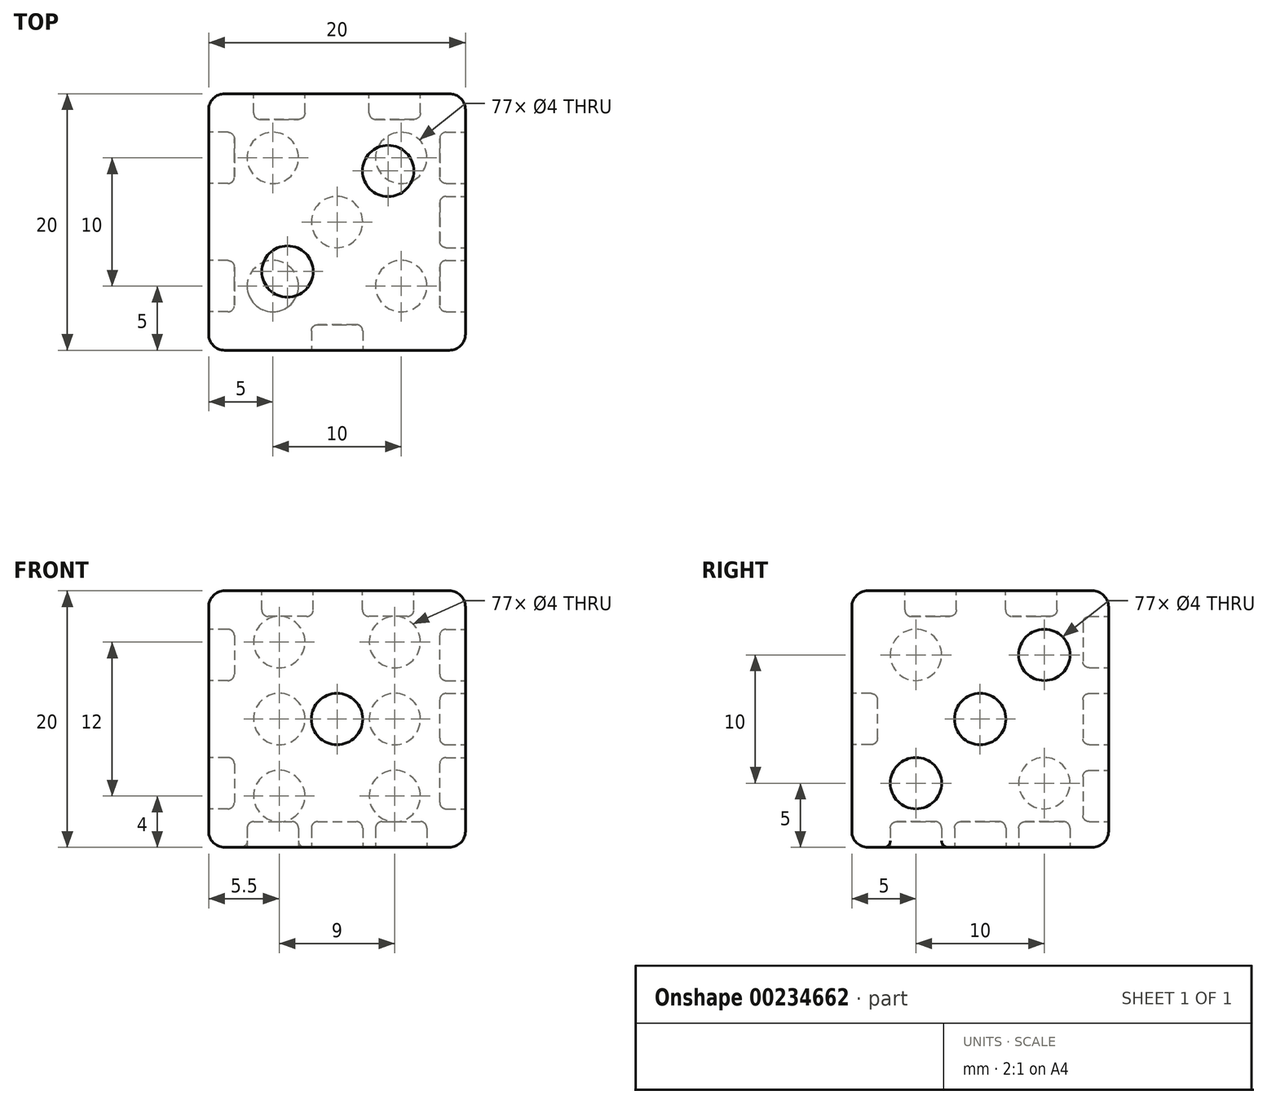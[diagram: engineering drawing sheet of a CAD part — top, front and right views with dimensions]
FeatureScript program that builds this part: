
annotation { "Feature Type Name" : "Feature", "Feature Type Description" : "" }
export const myFeature = defineFeature(function(context is Context, id is Id, definition is map)
    precondition{}
    {
        {
            assignVariable(context, id + "F0", {"name" : "Size", "anyValue" : 20});
        }
        {
            assignVariable(context, id + "F1", {"name" : "HoleDepth", "anyValue" : 2});
        }
        {
            var Q0;
            Q0=qCreatedBy(makeId("Top.planeOp"),FACE);
            var sketch = newSketch(context, id + "F2", { "sketchPlane" : qUnion([Q0])});
            skLineSegment(sketch, "E0.bottom", {"start": v(10, 10) * mm, "end": v(-10, 10) * mm});
            skLineSegment(sketch, "E0.top", {"start": v(10, -10) * mm, "end": v(-10, -10) * mm});
            skLineSegment(sketch, "E0.left", {"start": v(10, 10) * mm, "end": v(10, -10) * mm});
            skLineSegment(sketch, "E0.right", {"start": v(-10, 10) * mm, "end": v(-10, -10) * mm});
            skPoint(sketch, "E0.middle", {"position": v(0, 0) * mm});
            skSolve(sketch);
        }
        {
            var Q0;
            Q0=makeQuery(id+"F2.imprint","IMPRINT",FACE,{"disambiguationData":[TD([[makeQuery(id+"F2.imprint","IMPRINT",EDGE,{"derivedFrom":sQuery(id+"F2.wireOp",EDGE,"E0.bottom")}),1.0]])]});
            extrude(context, id + "F3", {"entities" : qUnion([Q0]), "depth" : (getVariable(context, 'Size')) * mm});
        }
        {
            var Q0;
            Q0=makeQuery(id+"F3.opExtrude","SWEPT_FACE",FACE,{"disambiguationData":[OSD([sQuery(id+"F2.wireOp",EDGE,"E0.top")])]});
            var sketch = newSketch(context, id + "F4", { "sketchPlane" : qUnion([Q0])});
            skLineSegment(sketch, "E1", {"start": v(-10, 20) * mm, "end": v(10, 0) * mm, "construction": true});
            skLineSegment(sketch, "E2", {"start": v(10, 20) * mm, "end": v(-10, 0) * mm, "construction": true});
            skCircle(sketch, "E3", {"center": v(0, 10) * mm, "radius": 2 * mm});
            skSolve(sketch);
        }
        {
            var Q0;
            Q0=makeQuery(id+"F3.opExtrude","CAP_FACE",FACE,{"disambiguationData":[OSD([sQuery(id+"F2.wireOp",EDGE,"E0.bottom"),sQuery(id+"F2.wireOp",EDGE,"E0.top"),sQuery(id+"F2.wireOp",EDGE,"E0.left"),sQuery(id+"F2.wireOp",EDGE,"E0.right")])],"isStart":false});
            var sketch = newSketch(context, id + "F5", { "sketchPlane" : qUnion([Q0])});
            skCircle(sketch, "E4", {"center": v(3.98, 3.98) * mm, "radius": 2 * mm});
            skCircle(sketch, "E5", {"center": v(-3.86, -3.86) * mm, "radius": 2 * mm});
            skLineSegment(sketch, "E6", {"start": v(10, 10) * mm, "end": v(3.98, 3.98) * mm, "construction": true});
            skLineSegment(sketch, "E7", {"start": v(-3.86, -3.86) * mm, "end": v(-10, -10) * mm, "construction": true});
            skLineSegment(sketch, "E8", {"start": v(-3.86, -3.86) * mm, "end": v(3.98, 3.98) * mm, "construction": true});
            skSolve(sketch);
        }
        {
            var Q0;
            Q0=makeQuery(id+"F3.opExtrude","SWEPT_FACE",FACE,{"disambiguationData":[OSD([sQuery(id+"F2.wireOp",EDGE,"E0.bottom")])]});
            var sketch = newSketch(context, id + "F6", { "sketchPlane" : qUnion([Q0])});
            skLineSegment(sketch, "E9.bottom", {"start": v(-4.5, 16) * mm, "end": v(4.5, 16) * mm, "construction": true});
            skLineSegment(sketch, "E9.top", {"start": v(-4.5, 4) * mm, "end": v(4.5, 4) * mm, "construction": true});
            skLineSegment(sketch, "E9.left", {"start": v(-4.5, 16) * mm, "end": v(-4.5, 4) * mm, "construction": true});
            skLineSegment(sketch, "E9.right", {"start": v(4.5, 16) * mm, "end": v(4.5, 4) * mm, "construction": true});
            skLineSegment(sketch, "E10", {"start": v(4.5, 16) * mm, "end": v(10, 20) * mm, "construction": true});
            skLineSegment(sketch, "E11", {"start": v(-4.5, 16) * mm, "end": v(-10, 20) * mm, "construction": true});
            skLineSegment(sketch, "E12", {"start": v(-4.5, 4) * mm, "end": v(-10, 0) * mm, "construction": true});
            skLineSegment(sketch, "E13", {"start": v(4.5, 4) * mm, "end": v(10, 0) * mm, "construction": true});
            skCircle(sketch, "E14", {"center": v(4.5, 4) * mm, "radius": 2 * mm});
            skCircle(sketch, "E15", {"center": v(4.5, 16) * mm, "radius": 2 * mm});
            skCircle(sketch, "E16", {"center": v(-4.5, 16) * mm, "radius": 2 * mm});
            skCircle(sketch, "E17", {"center": v(-4.5, 4) * mm, "radius": 2 * mm});
            skCircle(sketch, "E18", {"center": v(-4.5, 10) * mm, "radius": 2 * mm});
            skCircle(sketch, "E19", {"center": v(4.5, 10) * mm, "radius": 2 * mm});
            skSolve(sketch);
        }
        {
            var Q0;
            Q0=makeQuery(id+"F3.opExtrude","CAP_FACE",FACE,{"disambiguationData":[OSD([sQuery(id+"F2.wireOp",EDGE,"E0.bottom"),sQuery(id+"F2.wireOp",EDGE,"E0.top"),sQuery(id+"F2.wireOp",EDGE,"E0.left"),sQuery(id+"F2.wireOp",EDGE,"E0.right")])],"isStart":true});
            var sketch = newSketch(context, id + "F7", { "sketchPlane" : qUnion([Q0])});
            skCircle(sketch, "E20", {"center": v(0, 0) * mm, "radius": 2 * mm});
            skCircle(sketch, "E21", {"center": v(5, 5) * mm, "radius": 2 * mm});
            skCircle(sketch, "E22", {"center": v(-5, 5) * mm, "radius": 2 * mm});
            skCircle(sketch, "E23", {"center": v(-5, -5) * mm, "radius": 2 * mm});
            skCircle(sketch, "E24", {"center": v(5, -5) * mm, "radius": 2 * mm});
            skLineSegment(sketch, "E25", {"start": v(10, -10) * mm, "end": v(5, -5) * mm, "construction": true});
            skLineSegment(sketch, "E26", {"start": v(0, 0) * mm, "end": v(5, -5) * mm, "construction": true});
            skLineSegment(sketch, "E27", {"start": v(0, 0) * mm, "end": v(-5, 5) * mm, "construction": true});
            skLineSegment(sketch, "E28", {"start": v(-10, 10) * mm, "end": v(-5, 5) * mm, "construction": true});
            skLineSegment(sketch, "E29", {"start": v(10, 10) * mm, "end": v(5, 5) * mm, "construction": true});
            skLineSegment(sketch, "E30", {"start": v(0, 0) * mm, "end": v(5, 5) * mm, "construction": true});
            skLineSegment(sketch, "E31", {"start": v(0, 0) * mm, "end": v(-5, -5) * mm, "construction": true});
            skLineSegment(sketch, "E32", {"start": v(-5, -5) * mm, "end": v(-10, -10) * mm, "construction": true});
            skSolve(sketch);
        }
        {
            var Q0;
            Q0=makeQuery(id+"F3.opExtrude","SWEPT_FACE",FACE,{"disambiguationData":[OSD([sQuery(id+"F2.wireOp",EDGE,"E0.left")])]});
            var sketch = newSketch(context, id + "F8", { "sketchPlane" : qUnion([Q0])});
            skCircle(sketch, "E33", {"center": v(0, 10) * mm, "radius": 2 * mm});
            skCircle(sketch, "E34", {"center": v(5, 15) * mm, "radius": 2 * mm});
            skCircle(sketch, "E35", {"center": v(-5, 5) * mm, "radius": 2 * mm});
            skLineSegment(sketch, "E36", {"start": v(10, 20) * mm, "end": v(5, 15) * mm, "construction": true});
            skLineSegment(sketch, "E37", {"start": v(0, 10) * mm, "end": v(5, 15) * mm, "construction": true});
            skLineSegment(sketch, "E38", {"start": v(0, 10) * mm, "end": v(-5, 5) * mm, "construction": true});
            skLineSegment(sketch, "E39", {"start": v(-5, 5) * mm, "end": v(-10, 0) * mm, "construction": true});
            skSolve(sketch);
        }
        {
            var Q0;
            Q0=makeQuery(id+"F3.opExtrude","SWEPT_FACE",FACE,{"disambiguationData":[OSD([sQuery(id+"F2.wireOp",EDGE,"E0.right")])]});
            var sketch = newSketch(context, id + "F9", { "sketchPlane" : qUnion([Q0])});
            skLineSegment(sketch, "E40", {"start": v(10, 20) * mm, "end": v(-10, 0) * mm, "construction": true});
            skLineSegment(sketch, "E41", {"start": v(-10, 20) * mm, "end": v(10, 0) * mm, "construction": true});
            skLineSegment(sketch, "E42.bottom", {"start": v(-5, 15) * mm, "end": v(5, 15) * mm, "construction": true});
            skLineSegment(sketch, "E42.top", {"start": v(-5, 5) * mm, "end": v(5, 5) * mm, "construction": true});
            skLineSegment(sketch, "E42.left", {"start": v(-5, 15) * mm, "end": v(-5, 5) * mm, "construction": true});
            skLineSegment(sketch, "E42.right", {"start": v(5, 15) * mm, "end": v(5, 5) * mm, "construction": true});
            skPoint(sketch, "E42.middle", {"position": v(0, 10) * mm});
            skCircle(sketch, "E43", {"center": v(5, 15) * mm, "radius": 2 * mm});
            skCircle(sketch, "E44", {"center": v(5, 5) * mm, "radius": 2 * mm});
            skCircle(sketch, "E45", {"center": v(-5, 5) * mm, "radius": 2 * mm});
            skCircle(sketch, "E46", {"center": v(-5, 15) * mm, "radius": 2 * mm});
            skLineSegment(sketch, "E47", {"start": v(10, 10) * mm, "end": v(5, 5) * mm, "construction": true});
            skLineSegment(sketch, "E48", {"start": v(0, 0) * mm, "end": v(5, 5) * mm, "construction": true});
            skSolve(sketch);
        }
        {
            var Q0;
            Q0=makeQuery(id+"F4.imprint","IMPRINT",FACE,{"disambiguationData":[TD([[makeQuery(id+"F4.imprint","IMPRINT",EDGE,{"derivedFrom":sQuery(id+"F4.wireOp",EDGE,"E3")}),1.0]])]});
            extrude(context, id + "F10", {"entities" : qUnion([Q0]), "operationType" : NewBodyOperationType.REMOVE, "oppositeDirection" : true, "depth" : (getVariable(context, 'HoleDepth')) * mm});
        }
        {
            var Q0;
            Q0=makeQuery(id+"F5.imprint","IMPRINT",FACE,{"disambiguationData":[TD([[makeQuery(id+"F5.imprint","IMPRINT",EDGE,{"derivedFrom":sQuery(id+"F5.wireOp",EDGE,"E5")}),1.0]])]});
            var Q1;
            Q1=makeQuery(id+"F5.imprint","IMPRINT",FACE,{"disambiguationData":[TD([[makeQuery(id+"F5.imprint","IMPRINT",EDGE,{"derivedFrom":sQuery(id+"F5.wireOp",EDGE,"E4")}),1.0]])]});
            extrude(context, id + "F11", {"entities" : qUnion([Q0, Q1]), "operationType" : NewBodyOperationType.REMOVE, "oppositeDirection" : true, "depth" : (getVariable(context, 'HoleDepth')) * mm});
        }
        {
            var Q0;
            Q0=makeQuery(id+"F8.imprint","IMPRINT",FACE,{"disambiguationData":[TD([[makeQuery(id+"F8.imprint","IMPRINT",EDGE,{"derivedFrom":sQuery(id+"F8.wireOp",EDGE,"E35")}),1.0]])]});
            var Q1;
            Q1=makeQuery(id+"F8.imprint","IMPRINT",FACE,{"disambiguationData":[TD([[makeQuery(id+"F8.imprint","IMPRINT",EDGE,{"derivedFrom":sQuery(id+"F8.wireOp",EDGE,"E34")}),1.0]])]});
            var Q2;
            Q2=makeQuery(id+"F8.imprint","IMPRINT",FACE,{"disambiguationData":[TD([[makeQuery(id+"F8.imprint","IMPRINT",EDGE,{"derivedFrom":sQuery(id+"F8.wireOp",EDGE,"E33")}),1.0]])]});
            extrude(context, id + "F12", {"entities" : qUnion([Q0, Q1, Q2]), "operationType" : NewBodyOperationType.REMOVE, "oppositeDirection" : true, "depth" : (getVariable(context, 'HoleDepth')) * mm});
        }
        {
            var Q0;
            Q0=makeQuery(id+"F9.imprint","IMPRINT",FACE,{"disambiguationData":[TD([[makeQuery(id+"F9.imprint","IMPRINT",EDGE,{"derivedFrom":sQuery(id+"F9.wireOp",EDGE,"E46")}),1.0]])]});
            var Q1;
            Q1=makeQuery(id+"F9.imprint","IMPRINT",FACE,{"disambiguationData":[TD([[makeQuery(id+"F9.imprint","IMPRINT",EDGE,{"derivedFrom":sQuery(id+"F9.wireOp",EDGE,"E43")}),1.0]])]});
            var Q2;
            Q2=makeQuery(id+"F9.imprint","IMPRINT",FACE,{"disambiguationData":[TD([[makeQuery(id+"F9.imprint","IMPRINT",EDGE,{"derivedFrom":sQuery(id+"F9.wireOp",EDGE,"E44")}),1.0]])]});
            var Q3;
            Q3=makeQuery(id+"F9.imprint","IMPRINT",FACE,{"disambiguationData":[TD([[makeQuery(id+"F9.imprint","IMPRINT",EDGE,{"derivedFrom":sQuery(id+"F9.wireOp",EDGE,"E45")}),1.0]])]});
            extrude(context, id + "F13", {"entities" : qUnion([Q0, Q1, Q2, Q3]), "operationType" : NewBodyOperationType.REMOVE, "oppositeDirection" : true, "offsetDistance" : 25 * mm, "depth" : (getVariable(context, 'HoleDepth')) * mm});
        }
        {
            var Q0;
            Q0=makeQuery(id+"F7.imprint","IMPRINT",FACE,{"disambiguationData":[TD([[makeQuery(id+"F7.imprint","IMPRINT",EDGE,{"derivedFrom":sQuery(id+"F7.wireOp",EDGE,"E23")}),1.0]])]});
            var Q1;
            Q1=makeQuery(id+"F7.imprint","IMPRINT",FACE,{"disambiguationData":[TD([[makeQuery(id+"F7.imprint","IMPRINT",EDGE,{"derivedFrom":sQuery(id+"F7.wireOp",EDGE,"E24")}),1.0]])]});
            var Q2;
            Q2=makeQuery(id+"F7.imprint","IMPRINT",FACE,{"disambiguationData":[TD([[makeQuery(id+"F7.imprint","IMPRINT",EDGE,{"derivedFrom":sQuery(id+"F7.wireOp",EDGE,"E20")}),1.0]])]});
            var Q3;
            Q3=makeQuery(id+"F7.imprint","IMPRINT",FACE,{"disambiguationData":[TD([[makeQuery(id+"F7.imprint","IMPRINT",EDGE,{"derivedFrom":sQuery(id+"F7.wireOp",EDGE,"E22")}),1.0]])]});
            var Q4;
            Q4=makeQuery(id+"F7.imprint","IMPRINT",FACE,{"disambiguationData":[TD([[makeQuery(id+"F7.imprint","IMPRINT",EDGE,{"derivedFrom":sQuery(id+"F7.wireOp",EDGE,"E21")}),1.0]])]});
            extrude(context, id + "F14", {"entities" : qUnion([Q0, Q1, Q2, Q3, Q4]), "operationType" : NewBodyOperationType.REMOVE, "oppositeDirection" : true, "offsetDistance" : 25 * mm, "depth" : (getVariable(context, 'HoleDepth')) * mm});
        }
        {
            var Q0;
            Q0=makeQuery(id+"F6.imprint","IMPRINT",FACE,{"disambiguationData":[TD([[makeQuery(id+"F6.imprint","IMPRINT",EDGE,{"derivedFrom":sQuery(id+"F6.wireOp",EDGE,"E15")}),1.0]])]});
            var Q1;
            Q1=makeQuery(id+"F6.imprint","IMPRINT",FACE,{"disambiguationData":[TD([[makeQuery(id+"F6.imprint","IMPRINT",EDGE,{"derivedFrom":sQuery(id+"F6.wireOp",EDGE,"E19")}),1.0]])]});
            var Q2;
            Q2=makeQuery(id+"F6.imprint","IMPRINT",FACE,{"disambiguationData":[TD([[makeQuery(id+"F6.imprint","IMPRINT",EDGE,{"derivedFrom":sQuery(id+"F6.wireOp",EDGE,"E14")}),1.0]])]});
            var Q3;
            Q3=makeQuery(id+"F6.imprint","IMPRINT",FACE,{"disambiguationData":[TD([[makeQuery(id+"F6.imprint","IMPRINT",EDGE,{"derivedFrom":sQuery(id+"F6.wireOp",EDGE,"E17")}),1.0]])]});
            var Q4;
            Q4=makeQuery(id+"F6.imprint","IMPRINT",FACE,{"disambiguationData":[TD([[makeQuery(id+"F6.imprint","IMPRINT",EDGE,{"derivedFrom":sQuery(id+"F6.wireOp",EDGE,"E18")}),1.0]])]});
            var Q5;
            Q5=makeQuery(id+"F6.imprint","IMPRINT",FACE,{"disambiguationData":[TD([[makeQuery(id+"F6.imprint","IMPRINT",EDGE,{"derivedFrom":sQuery(id+"F6.wireOp",EDGE,"E16")}),1.0]])]});
            extrude(context, id + "F15", {"entities" : qUnion([Q0, Q1, Q2, Q3, Q4, Q5]), "operationType" : NewBodyOperationType.REMOVE, "oppositeDirection" : true, "depth" : (getVariable(context, 'HoleDepth')) * mm});
        }
        {
            var Q0;
            Q0=makeQuery(id+"F11.boolean.opBoolean","COPY",EDGE,{"derivedFrom":makeQuery(id+"F11.opExtrude","CAP_EDGE",EDGE,{"disambiguationData":[OSD([sQuery(id+"F5.wireOp",EDGE,"E4")])],"isStart":true})});
            var Q1;
            Q1=makeQuery(id+"F11.boolean.opBoolean","COPY",EDGE,{"derivedFrom":makeQuery(id+"F11.opExtrude","CAP_EDGE",EDGE,{"disambiguationData":[OSD([sQuery(id+"F5.wireOp",EDGE,"E5")])],"isStart":true})});
            var Q2;
            Q2=makeQuery(id+"F11.boolean.opBoolean","COPY",EDGE,{"derivedFrom":makeQuery(id+"F11.opExtrude","CAP_EDGE",EDGE,{"disambiguationData":[OSD([sQuery(id+"F5.wireOp",EDGE,"E4")])],"isStart":false})});
            var Q3;
            Q3=makeQuery(id+"F11.boolean.opBoolean","COPY",EDGE,{"derivedFrom":makeQuery(id+"F11.opExtrude","CAP_EDGE",EDGE,{"disambiguationData":[OSD([sQuery(id+"F5.wireOp",EDGE,"E5")])],"isStart":false})});
            var Q4;
            Q4=makeQuery(id+"F10.boolean.opBoolean","COPY",EDGE,{"derivedFrom":makeQuery(id+"F10.opExtrude","CAP_EDGE",EDGE,{"disambiguationData":[OSD([sQuery(id+"F4.wireOp",EDGE,"E3")])],"isStart":false})});
            var Q5;
            Q5=makeQuery(id+"F10.boolean.opBoolean","COPY",EDGE,{"derivedFrom":makeQuery(id+"F10.opExtrude","CAP_EDGE",EDGE,{"disambiguationData":[OSD([sQuery(id+"F4.wireOp",EDGE,"E3")])],"isStart":true})});
            var Q6;
            Q6=makeQuery(id+"F12.boolean.opBoolean","COPY",EDGE,{"derivedFrom":makeQuery(id+"F12.opExtrude","CAP_EDGE",EDGE,{"disambiguationData":[OSD([sQuery(id+"F8.wireOp",EDGE,"E34")])],"isStart":false})});
            var Q7;
            Q7=makeQuery(id+"F12.boolean.opBoolean","COPY",EDGE,{"derivedFrom":makeQuery(id+"F12.opExtrude","CAP_EDGE",EDGE,{"disambiguationData":[OSD([sQuery(id+"F8.wireOp",EDGE,"E34")])],"isStart":true})});
            var Q8;
            Q8=makeQuery(id+"F12.boolean.opBoolean","COPY",EDGE,{"derivedFrom":makeQuery(id+"F12.opExtrude","CAP_EDGE",EDGE,{"disambiguationData":[OSD([sQuery(id+"F8.wireOp",EDGE,"E33")])],"isStart":false})});
            var Q9;
            Q9=makeQuery(id+"F12.boolean.opBoolean","COPY",EDGE,{"derivedFrom":makeQuery(id+"F12.opExtrude","CAP_EDGE",EDGE,{"disambiguationData":[OSD([sQuery(id+"F8.wireOp",EDGE,"E33")])],"isStart":true})});
            var Q10;
            Q10=makeQuery(id+"F12.boolean.opBoolean","COPY",EDGE,{"derivedFrom":makeQuery(id+"F12.opExtrude","CAP_EDGE",EDGE,{"disambiguationData":[OSD([sQuery(id+"F8.wireOp",EDGE,"E35")])],"isStart":false})});
            var Q11;
            Q11=makeQuery(id+"F12.boolean.opBoolean","COPY",EDGE,{"derivedFrom":makeQuery(id+"F12.opExtrude","CAP_EDGE",EDGE,{"disambiguationData":[OSD([sQuery(id+"F8.wireOp",EDGE,"E35")])],"isStart":true})});
            var Q12;
            Q12=makeQuery(id+"F15.boolean.opBoolean","COPY",EDGE,{"derivedFrom":makeQuery(id+"F15.opExtrude","CAP_EDGE",EDGE,{"disambiguationData":[OSD([sQuery(id+"F6.wireOp",EDGE,"E16")])],"isStart":false})});
            var Q13;
            Q13=makeQuery(id+"F15.boolean.opBoolean","COPY",EDGE,{"derivedFrom":makeQuery(id+"F15.opExtrude","CAP_EDGE",EDGE,{"disambiguationData":[OSD([sQuery(id+"F6.wireOp",EDGE,"E15")])],"isStart":false})});
            var Q14;
            Q14=makeQuery(id+"F15.boolean.opBoolean","COPY",EDGE,{"derivedFrom":makeQuery(id+"F15.opExtrude","CAP_EDGE",EDGE,{"disambiguationData":[OSD([sQuery(id+"F6.wireOp",EDGE,"E15")])],"isStart":true})});
            var Q15;
            Q15=makeQuery(id+"F15.boolean.opBoolean","COPY",EDGE,{"derivedFrom":makeQuery(id+"F15.opExtrude","CAP_EDGE",EDGE,{"disambiguationData":[OSD([sQuery(id+"F6.wireOp",EDGE,"E16")])],"isStart":true})});
            var Q16;
            Q16=makeQuery(id+"F15.boolean.opBoolean","COPY",EDGE,{"derivedFrom":makeQuery(id+"F15.opExtrude","CAP_EDGE",EDGE,{"disambiguationData":[OSD([sQuery(id+"F6.wireOp",EDGE,"E18")])],"isStart":false})});
            var Q17;
            Q17=makeQuery(id+"F15.boolean.opBoolean","COPY",EDGE,{"derivedFrom":makeQuery(id+"F15.opExtrude","CAP_EDGE",EDGE,{"disambiguationData":[OSD([sQuery(id+"F6.wireOp",EDGE,"E18")])],"isStart":true})});
            var Q18;
            Q18=makeQuery(id+"F15.boolean.opBoolean","COPY",EDGE,{"derivedFrom":makeQuery(id+"F15.opExtrude","CAP_EDGE",EDGE,{"disambiguationData":[OSD([sQuery(id+"F6.wireOp",EDGE,"E19")])],"isStart":false})});
            var Q19;
            Q19=makeQuery(id+"F15.boolean.opBoolean","COPY",EDGE,{"derivedFrom":makeQuery(id+"F15.opExtrude","CAP_EDGE",EDGE,{"disambiguationData":[OSD([sQuery(id+"F6.wireOp",EDGE,"E19")])],"isStart":true})});
            var Q20;
            Q20=makeQuery(id+"F15.boolean.opBoolean","COPY",EDGE,{"derivedFrom":makeQuery(id+"F15.opExtrude","CAP_EDGE",EDGE,{"disambiguationData":[OSD([sQuery(id+"F6.wireOp",EDGE,"E14")])],"isStart":false})});
            var Q21;
            Q21=makeQuery(id+"F15.boolean.opBoolean","COPY",EDGE,{"derivedFrom":makeQuery(id+"F15.opExtrude","CAP_EDGE",EDGE,{"disambiguationData":[OSD([sQuery(id+"F6.wireOp",EDGE,"E14")])],"isStart":true})});
            var Q22;
            Q22=makeQuery(id+"F15.boolean.opBoolean","COPY",EDGE,{"derivedFrom":makeQuery(id+"F15.opExtrude","CAP_EDGE",EDGE,{"disambiguationData":[OSD([sQuery(id+"F6.wireOp",EDGE,"E17")])],"isStart":false})});
            var Q23;
            Q23=makeQuery(id+"F15.boolean.opBoolean","COPY",EDGE,{"derivedFrom":makeQuery(id+"F15.opExtrude","CAP_EDGE",EDGE,{"disambiguationData":[OSD([sQuery(id+"F6.wireOp",EDGE,"E17")])],"isStart":true})});
            var Q24;
            Q24=makeQuery(id+"F13.boolean.opBoolean","COPY",EDGE,{"derivedFrom":makeQuery(id+"F13.opExtrude","CAP_EDGE",EDGE,{"disambiguationData":[OSD([sQuery(id+"F9.wireOp",EDGE,"E46")])],"isStart":false})});
            var Q25;
            Q25=makeQuery(id+"F13.boolean.opBoolean","COPY",EDGE,{"derivedFrom":makeQuery(id+"F13.opExtrude","CAP_EDGE",EDGE,{"disambiguationData":[OSD([sQuery(id+"F9.wireOp",EDGE,"E46")])],"isStart":true})});
            var Q26;
            Q26=makeQuery(id+"F13.boolean.opBoolean","COPY",EDGE,{"derivedFrom":makeQuery(id+"F13.opExtrude","CAP_EDGE",EDGE,{"disambiguationData":[OSD([sQuery(id+"F9.wireOp",EDGE,"E43")])],"isStart":false})});
            var Q27;
            Q27=makeQuery(id+"F13.boolean.opBoolean","COPY",EDGE,{"derivedFrom":makeQuery(id+"F13.opExtrude","CAP_EDGE",EDGE,{"disambiguationData":[OSD([sQuery(id+"F9.wireOp",EDGE,"E43")])],"isStart":true})});
            var Q28;
            Q28=makeQuery(id+"F13.boolean.opBoolean","COPY",EDGE,{"derivedFrom":makeQuery(id+"F13.opExtrude","CAP_EDGE",EDGE,{"disambiguationData":[OSD([sQuery(id+"F9.wireOp",EDGE,"E45")])],"isStart":false})});
            var Q29;
            Q29=makeQuery(id+"F13.boolean.opBoolean","COPY",EDGE,{"derivedFrom":makeQuery(id+"F13.opExtrude","CAP_EDGE",EDGE,{"disambiguationData":[OSD([sQuery(id+"F9.wireOp",EDGE,"E45")])],"isStart":true})});
            var Q30;
            Q30=makeQuery(id+"F13.boolean.opBoolean","COPY",EDGE,{"derivedFrom":makeQuery(id+"F13.opExtrude","CAP_EDGE",EDGE,{"disambiguationData":[OSD([sQuery(id+"F9.wireOp",EDGE,"E44")])],"isStart":false})});
            var Q31;
            Q31=makeQuery(id+"F13.boolean.opBoolean","COPY",EDGE,{"derivedFrom":makeQuery(id+"F13.opExtrude","CAP_EDGE",EDGE,{"disambiguationData":[OSD([sQuery(id+"F9.wireOp",EDGE,"E44")])],"isStart":true})});
            var Q32;
            Q32=makeQuery(id+"F14.boolean.opBoolean","COPY",EDGE,{"derivedFrom":makeQuery(id+"F14.opExtrude","CAP_EDGE",EDGE,{"disambiguationData":[OSD([sQuery(id+"F7.wireOp",EDGE,"E23")])],"isStart":false})});
            var Q33;
            Q33=makeQuery(id+"F14.boolean.opBoolean","COPY",EDGE,{"derivedFrom":makeQuery(id+"F14.opExtrude","CAP_EDGE",EDGE,{"disambiguationData":[OSD([sQuery(id+"F7.wireOp",EDGE,"E23")])],"isStart":true})});
            var Q34;
            Q34=makeQuery(id+"F14.boolean.opBoolean","COPY",EDGE,{"derivedFrom":makeQuery(id+"F14.opExtrude","CAP_EDGE",EDGE,{"disambiguationData":[OSD([sQuery(id+"F7.wireOp",EDGE,"E20")])],"isStart":false})});
            var Q35;
            Q35=makeQuery(id+"F14.boolean.opBoolean","COPY",EDGE,{"derivedFrom":makeQuery(id+"F14.opExtrude","CAP_EDGE",EDGE,{"disambiguationData":[OSD([sQuery(id+"F7.wireOp",EDGE,"E20")])],"isStart":true})});
            var Q36;
            Q36=makeQuery(id+"F14.boolean.opBoolean","COPY",EDGE,{"derivedFrom":makeQuery(id+"F14.opExtrude","CAP_EDGE",EDGE,{"disambiguationData":[OSD([sQuery(id+"F7.wireOp",EDGE,"E22")])],"isStart":false})});
            var Q37;
            Q37=makeQuery(id+"F14.boolean.opBoolean","COPY",FACE,{"derivedFrom":makeQuery(id+"F14.opExtrude","SWEPT_FACE",FACE,{"disambiguationData":[OSD([sQuery(id+"F7.wireOp",EDGE,"E22")])]})});
            var Q38;
            Q38=makeQuery(id+"F14.boolean.opBoolean","COPY",EDGE,{"derivedFrom":makeQuery(id+"F14.opExtrude","CAP_EDGE",EDGE,{"disambiguationData":[OSD([sQuery(id+"F7.wireOp",EDGE,"E21")])],"isStart":false})});
            var Q39;
            Q39=makeQuery(id+"F14.boolean.opBoolean","COPY",EDGE,{"derivedFrom":makeQuery(id+"F14.opExtrude","CAP_EDGE",EDGE,{"disambiguationData":[OSD([sQuery(id+"F7.wireOp",EDGE,"E21")])],"isStart":true})});
            var Q40;
            Q40=makeQuery(id+"F14.boolean.opBoolean","COPY",EDGE,{"derivedFrom":makeQuery(id+"F14.opExtrude","CAP_EDGE",EDGE,{"disambiguationData":[OSD([sQuery(id+"F7.wireOp",EDGE,"E24")])],"isStart":false})});
            var Q41;
            Q41=makeQuery(id+"F14.boolean.opBoolean","COPY",EDGE,{"derivedFrom":makeQuery(id+"F14.opExtrude","CAP_EDGE",EDGE,{"disambiguationData":[OSD([sQuery(id+"F7.wireOp",EDGE,"E24")])],"isStart":true})});
            fillet(context, id + "F16", {"entities" : qUnion([Q0, Q1, Q2, Q3, Q4, Q5, Q6, Q7, Q8, Q9, Q10, Q11, Q12, Q13, Q14, Q15, Q16, Q17, Q18, Q19, Q20, Q21, Q22, Q23, Q24, Q25, Q26, Q27, Q28, Q29, Q30, Q31, Q32, Q33, Q34, Q35, Q36, Q37, Q38, Q39, Q40, Q41]), "radius" : .5 * mm, "tangentPropagation" : true, "allowEdgeOverflow" : false});
        }
        {
            var Q0;
            Q0=makeQuery(id+"F3.opExtrude","SWEPT_EDGE",EDGE,{"disambiguationData":[OSD([sQuery(id+"F2.wireOp",EDGE,"E0.bottom"),sQuery(id+"F2.wireOp",EDGE,"E0.left")])]});
            var Q1;
            Q1=makeQuery(id+"F3.opExtrude","CAP_EDGE",EDGE,{"disambiguationData":[OSD([sQuery(id+"F2.wireOp",EDGE,"E0.left")])],"isStart":true});
            var Q2;
            Q2=makeQuery(id+"F3.opExtrude","CAP_EDGE",EDGE,{"disambiguationData":[OSD([sQuery(id+"F2.wireOp",EDGE,"E0.bottom")])],"isStart":true});
            var Q3;
            Q3=makeQuery(id+"F3.opExtrude","CAP_EDGE",EDGE,{"disambiguationData":[OSD([sQuery(id+"F2.wireOp",EDGE,"E0.left")])],"isStart":false});
            var Q4;
            Q4=makeQuery(id+"F3.opExtrude","SWEPT_EDGE",EDGE,{"disambiguationData":[OSD([sQuery(id+"F2.wireOp",EDGE,"E0.top"),sQuery(id+"F2.wireOp",EDGE,"E0.left")])]});
            var Q5;
            Q5=makeQuery(id+"F3.opExtrude","CAP_EDGE",EDGE,{"disambiguationData":[OSD([sQuery(id+"F2.wireOp",EDGE,"E0.top")])],"isStart":true});
            var Q6;
            Q6=makeQuery(id+"F3.opExtrude","CAP_EDGE",EDGE,{"disambiguationData":[OSD([sQuery(id+"F2.wireOp",EDGE,"E0.right")])],"isStart":true});
            var Q7;
            Q7=makeQuery(id+"F3.opExtrude","CAP_EDGE",EDGE,{"disambiguationData":[OSD([sQuery(id+"F2.wireOp",EDGE,"E0.top")])],"isStart":false});
            var Q8;
            Q8=makeQuery(id+"F3.opExtrude","SWEPT_EDGE",EDGE,{"disambiguationData":[OSD([sQuery(id+"F2.wireOp",EDGE,"E0.top"),sQuery(id+"F2.wireOp",EDGE,"E0.right")])]});
            var Q9;
            Q9=makeQuery(id+"F3.opExtrude","CAP_EDGE",EDGE,{"disambiguationData":[OSD([sQuery(id+"F2.wireOp",EDGE,"E0.right")])],"isStart":false});
            var Q10;
            Q10=makeQuery(id+"F3.opExtrude","CAP_EDGE",EDGE,{"disambiguationData":[OSD([sQuery(id+"F2.wireOp",EDGE,"E0.bottom")])],"isStart":false});
            var Q11;
            Q11=makeQuery(id+"F3.opExtrude","SWEPT_EDGE",EDGE,{"disambiguationData":[OSD([sQuery(id+"F2.wireOp",EDGE,"E0.bottom"),sQuery(id+"F2.wireOp",EDGE,"E0.right")])]});
            var Q12;
            Q12=makeQuery(id+"F16.opFillet","BLEND_EDGE",EDGE,{"blendedFrom":[makeQuery(id+"F14.boolean.opBoolean","COPY",EDGE,{"derivedFrom":makeQuery(id+"F14.opExtrude","CAP_EDGE",EDGE,{"disambiguationData":[OSD([sQuery(id+"F7.wireOp",EDGE,"E23")])],"isStart":true})}),makeQuery(id+"F3.opExtrude","CAP_FACE",FACE,{"disambiguationData":[OSD([sQuery(id+"F2.wireOp",EDGE,"E0.bottom"),sQuery(id+"F2.wireOp",EDGE,"E0.top"),sQuery(id+"F2.wireOp",EDGE,"E0.left"),sQuery(id+"F2.wireOp",EDGE,"E0.right")])],"isStart":true})],"blendedInto":[makeQuery(id+"F3.opExtrude","CAP_FACE",FACE,{"disambiguationData":[OSD([sQuery(id+"F2.wireOp",EDGE,"E0.bottom"),sQuery(id+"F2.wireOp",EDGE,"E0.top"),sQuery(id+"F2.wireOp",EDGE,"E0.left"),sQuery(id+"F2.wireOp",EDGE,"E0.right")])],"isStart":true})]});
            fillet(context, id + "F17", {"entities" : qUnion([Q0, Q1, Q2, Q3, Q4, Q5, Q6, Q7, Q8, Q9, Q10, Q11, Q12]), "radius" : 1.25 * mm, "tangentPropagation" : true, "allowEdgeOverflow" : false});
        }
    });
